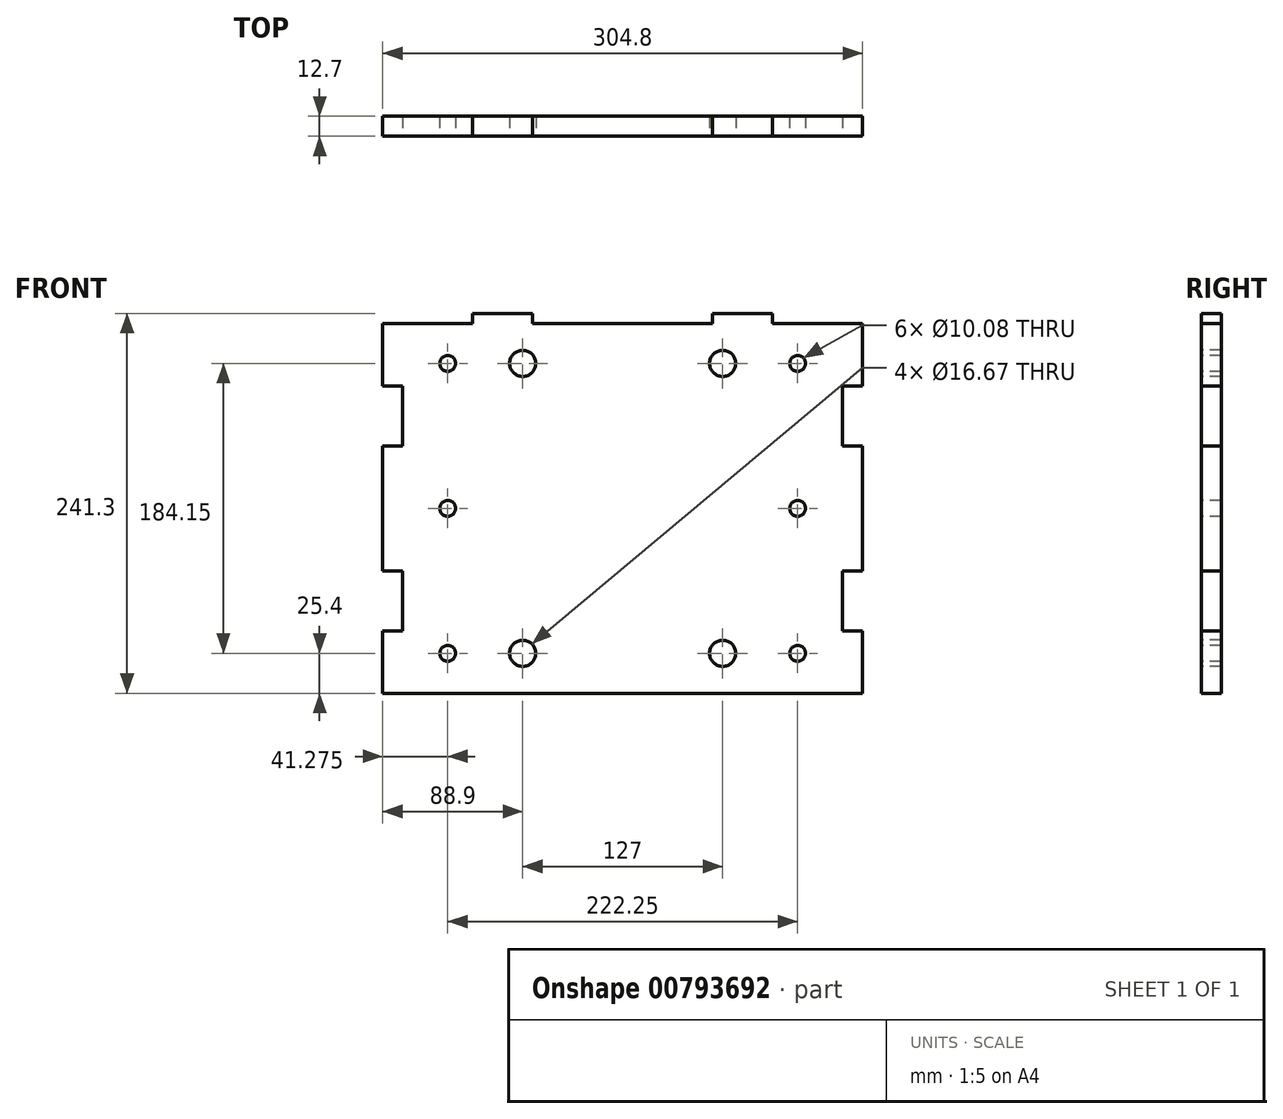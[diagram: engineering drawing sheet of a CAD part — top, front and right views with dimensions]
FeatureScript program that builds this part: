
annotation { "Feature Type Name" : "Feature", "Feature Type Description" : "" }
export const myFeature = defineFeature(function(context is Context, id is Id, definition is map)
    precondition{}
    {
        {
            var Q0;
            Q0=qCreatedBy(makeId("Front.planeOp"),FACE);
            var sketch = newSketch(context, id + "F0", { "sketchPlane" : qUnion([Q0])});
            skLineSegment(sketch, "E0.bottom", {"start": v(0, 0) * mm, "end": v(304.8, 0) * mm});
            skLineSegment(sketch, "E0.top", {"start": v(0, 234.95) * mm, "end": v(304.8, 234.95) * mm});
            skLineSegment(sketch, "E0.left", {"start": v(0, 0) * mm, "end": v(0, 234.95) * mm});
            skLineSegment(sketch, "E0.right", {"start": v(304.8, 0) * mm, "end": v(304.8, 234.95) * mm});
            skSolve(sketch);
        }
        {
            var Q0;
            Q0 = qSketchRegion(id + "F0", true);
            extrude(context, id + "F1", {"entities" : qUnion([Q0]), "depth" : 12.7 * mm, "offsetDistance" : 25.4 * mm});
        }
        {
            var Q0;
            Q0=makeQuery(id+"F1.opExtrude","CAP_FACE",FACE,{"disambiguationData":[OSD([sQuery(id+"F0.wireOp",EDGE,"E0.bottom"),sQuery(id+"F0.wireOp",EDGE,"E0.top"),sQuery(id+"F0.wireOp",EDGE,"E0.left"),sQuery(id+"F0.wireOp",EDGE,"E0.right")])],"isStart":false});
            var sketch = newSketch(context, id + "F2", { "sketchPlane" : qUnion([Q0])});
            skLineSegment(sketch, "E1", {"start": v(152.4, 0) * mm, "end": v(152.4, 234.95) * mm, "construction": true});
            skLineSegment(sketch, "E2", {"start": v(0, 25.4) * mm, "end": v(304.8, 25.4) * mm, "construction": true});
            skLineSegment(sketch, "E3", {"start": v(0, 209.55) * mm, "end": v(304.8, 209.55) * mm, "construction": true});
            skPoint(sketch, "E4", {"position": v(88.9, 209.55) * mm});
            skPoint(sketch, "E5", {"position": v(88.9, 25.4) * mm});
            skPoint(sketch, "E6.MirrorP", {"position": v(215.9, 25.4) * mm});
            skPoint(sketch, "E7.MirrorP", {"position": v(215.9, 209.55) * mm});
            skSolve(sketch);
        }
        {
            var Q0;
            Q0=sQuery(id+"F2.wireOp",VERTEX,"E6.MirrorP");
            var Q1;
            Q1=sQuery(id+"F2.wireOp",VERTEX,"E5");
            var Q2;
            Q2=sQuery(id+"F2.wireOp",VERTEX,"E4");
            var Q3;
            Q3=sQuery(id+"F2.wireOp",VERTEX,"E7.MirrorP");
            var Q4;
            Q4=makeQuery(id+"F1.opExtrude","SWEPT_BODY",BODY,{"disambiguationData":[OSD([sQuery(id+"F0.wireOp",EDGE,"E0.bottom"),sQuery(id+"F0.wireOp",EDGE,"E0.top"),sQuery(id+"F0.wireOp",EDGE,"E0.left"),sQuery(id+"F0.wireOp",EDGE,"E0.right")])]});
            hole(context, id + "F3", {"style" : HoleStyle.SIMPLE, "endStyle" : HoleEndStyle.THROUGH, "standardTappedOrClearance" : lookupTablePath({ "fit" : "Normal (ASME)", "standard" : "ANSI", "size" : "5/8", "type" : "Clearance" }), "standardBlindInLast" : lookupTablePath({ "fit" : "Free", "standard" : "ANSI", "size" : "5/8", "type" : "Clearance" }), "holeDiameter" : 16.67 * mm, "majorDiameter" : 6.35 * mm, "isTappedThrough" : true, "tappedDepth" : 12.7 * mm, "tapClearance" : 3, "locations" : qUnion([Q0, Q1, Q2, Q3]), "scope" : qUnion([Q4])});
        }
        {
            var Q0;
            Q0=makeQuery(id+"F1.opExtrude","CAP_FACE",FACE,{"disambiguationData":[OSD([sQuery(id+"F0.wireOp",EDGE,"E0.bottom"),sQuery(id+"F0.wireOp",EDGE,"E0.top"),sQuery(id+"F0.wireOp",EDGE,"E0.left"),sQuery(id+"F0.wireOp",EDGE,"E0.right")])],"isStart":false});
            var sketch = newSketch(context, id + "F4", { "sketchPlane" : qUnion([Q0])});
            skLineSegment(sketch, "E8", {"start": v(152.4, 234.95) * mm, "end": v(152.4, 0) * mm, "construction": true});
            skLineSegment(sketch, "E9", {"start": v(263.52, 234.95) * mm, "end": v(263.53, 0) * mm, "construction": true});
            skPoint(sketch, "E10", {"position": v(263.53, 209.55) * mm});
            skPoint(sketch, "E11", {"position": v(263.53, 25.4) * mm});
            skPoint(sketch, "E12", {"position": v(263.53, 117.47) * mm});
            skPoint(sketch, "E13.MirrorP", {"position": v(41.27, 25.4) * mm});
            skPoint(sketch, "E14.MirrorP", {"position": v(41.27, 117.47) * mm});
            skPoint(sketch, "E15.MirrorP", {"position": v(41.28, 209.55) * mm});
            skSolve(sketch);
        }
        {
            var Q0;
            Q0=sQuery(id+"F4.wireOp",VERTEX,"E11");
            var Q1;
            Q1=sQuery(id+"F4.wireOp",VERTEX,"E10");
            var Q2;
            Q2=sQuery(id+"F4.wireOp",VERTEX,"E15.MirrorP");
            var Q3;
            Q3=sQuery(id+"F4.wireOp",VERTEX,"E13.MirrorP");
            var Q4;
            Q4=sQuery(id+"F4.wireOp",VERTEX,"E14.MirrorP");
            var Q5;
            Q5=sQuery(id+"F4.wireOp",VERTEX,"E12");
            var Q6;
            Q6=makeQuery(id+"F1.opExtrude","SWEPT_BODY",BODY,{"disambiguationData":[OSD([sQuery(id+"F0.wireOp",EDGE,"E0.bottom"),sQuery(id+"F0.wireOp",EDGE,"E0.top"),sQuery(id+"F0.wireOp",EDGE,"E0.left"),sQuery(id+"F0.wireOp",EDGE,"E0.right")])]});
            hole(context, id + "F5", {"style" : HoleStyle.SIMPLE, "endStyle" : HoleEndStyle.THROUGH, "standardTappedOrClearance" : lookupTablePath({ "fit" : "Normal (ASME)", "standard" : "ANSI", "size" : "3/8", "type" : "Clearance" }), "standardBlindInLast" : lookupTablePath({ "fit" : "Free", "standard" : "ANSI", "size" : "3/8", "type" : "Clearance" }), "holeDiameter" : 10.08 * mm, "majorDiameter" : 6.35 * mm, "isTappedThrough" : true, "tappedDepth" : 12.7 * mm, "tapClearance" : 3, "locations" : qUnion([Q0, Q1, Q2, Q3, Q4, Q5]), "scope" : qUnion([Q6])});
        }
        {
            var Q0;
            Q0=makeQuery(id+"F1.opExtrude","CAP_FACE",FACE,{"disambiguationData":[OSD([sQuery(id+"F0.wireOp",EDGE,"E0.bottom"),sQuery(id+"F0.wireOp",EDGE,"E0.top"),sQuery(id+"F0.wireOp",EDGE,"E0.left"),sQuery(id+"F0.wireOp",EDGE,"E0.right")])],"isStart":false});
            var sketch = newSketch(context, id + "F6", { "sketchPlane" : qUnion([Q0])});
            skLineSegment(sketch, "E16", {"start": v(0, 117.47) * mm, "end": v(304.8, 117.47) * mm, "construction": true});
            skLineSegment(sketch, "E17", {"start": v(152.4, 234.95) * mm, "end": v(152.4, 0) * mm, "construction": true});
            skLineSegment(sketch, "E18.bottom", {"start": v(304.8, 195.26) * mm, "end": v(292.1, 195.26) * mm});
            skLineSegment(sketch, "E18.top", {"start": v(304.8, 157.16) * mm, "end": v(292.1, 157.16) * mm});
            skLineSegment(sketch, "E18.left", {"start": v(304.8, 195.26) * mm, "end": v(304.8, 157.16) * mm});
            skLineSegment(sketch, "E18.right", {"start": v(292.1, 195.26) * mm, "end": v(292.1, 157.16) * mm});
            skLineSegment(sketch, "E19.MirrorCS", {"start": v(304.8, 39.69) * mm, "end": v(304.8, 77.79) * mm});
            skLineSegment(sketch, "E20.MirrorCS", {"start": v(292.1, 39.69) * mm, "end": v(292.1, 77.79) * mm});
            skLineSegment(sketch, "E21.MirrorCS", {"start": v(304.8, 77.79) * mm, "end": v(292.1, 77.79) * mm});
            skLineSegment(sketch, "E22.MirrorCS", {"start": v(304.8, 39.69) * mm, "end": v(292.1, 39.69) * mm});
            skLineSegment(sketch, "E23.MirrorCS", {"start": v(0, 77.79) * mm, "end": v(12.7, 77.79) * mm});
            skLineSegment(sketch, "E24.MirrorCS", {"start": v(12.7, 39.69) * mm, "end": v(12.7, 77.79) * mm});
            skLineSegment(sketch, "E25.MirrorCS", {"start": v(0, 39.69) * mm, "end": v(0, 77.79) * mm});
            skLineSegment(sketch, "E26.MirrorCS", {"start": v(0, 39.69) * mm, "end": v(12.7, 39.69) * mm});
            skLineSegment(sketch, "E27.MirrorCS", {"start": v(0, 157.16) * mm, "end": v(12.7, 157.16) * mm});
            skLineSegment(sketch, "E28.MirrorCS", {"start": v(0, 195.26) * mm, "end": v(0, 157.16) * mm});
            skLineSegment(sketch, "E29.MirrorCS", {"start": v(12.7, 195.26) * mm, "end": v(12.7, 157.16) * mm});
            skLineSegment(sketch, "E30.MirrorCS", {"start": v(0, 195.26) * mm, "end": v(12.7, 195.26) * mm});
            skSolve(sketch);
        }
        {
            var Q0;
            Q0=makeQuery(id+"F6.imprint","IMPRINT",FACE,{"disambiguationData":[TD([[makeQuery(id+"F6.imprint","IMPRINT",EDGE,{"derivedFrom":sQuery(id+"F6.wireOp",EDGE,"E21.MirrorCS")}),1.0]])]});
            var Q1;
            Q1=makeQuery(id+"F6.imprint","IMPRINT",FACE,{"disambiguationData":[TD([[makeQuery(id+"F6.imprint","IMPRINT",EDGE,{"derivedFrom":sQuery(id+"F6.wireOp",EDGE,"E23.MirrorCS")}),-1.0]])]});
            var Q2;
            Q2=makeQuery(id+"F6.imprint","IMPRINT",FACE,{"disambiguationData":[TD([[makeQuery(id+"F6.imprint","IMPRINT",EDGE,{"derivedFrom":sQuery(id+"F6.wireOp",EDGE,"E27.MirrorCS")}),1.0]])]});
            var Q3;
            Q3=makeQuery(id+"F6.imprint","IMPRINT",FACE,{"disambiguationData":[TD([[makeQuery(id+"F6.imprint","IMPRINT",EDGE,{"derivedFrom":sQuery(id+"F6.wireOp",EDGE,"E18.bottom")}),1.0]])]});
            extrude(context, id + "F7", {"entities" : qUnion([Q0, Q1, Q2, Q3]), "operationType" : NewBodyOperationType.REMOVE, "oppositeDirection" : true, "depth" : 25.4 * mm, "offsetDistance" : 25.4 * mm});
        }
        {
            var Q0;
            Q0=makeQuery(id+"F1.opExtrude","CAP_FACE",FACE,{"disambiguationData":[OSD([sQuery(id+"F0.wireOp",EDGE,"E0.bottom"),sQuery(id+"F0.wireOp",EDGE,"E0.top"),sQuery(id+"F0.wireOp",EDGE,"E0.left"),sQuery(id+"F0.wireOp",EDGE,"E0.right")])],"isStart":false});
            var sketch = newSketch(context, id + "F8", { "sketchPlane" : qUnion([Q0])});
            skLineSegment(sketch, "E31", {"start": v(152.4, 234.95) * mm, "end": v(152.4, 0) * mm, "construction": true});
            skLineSegment(sketch, "E32", {"start": v(0, 117.48) * mm, "end": v(304.8, 117.47) * mm, "construction": true});
            skLineSegment(sketch, "E33.MirrorCS", {"start": v(95.25, 234.95) * mm, "end": v(57.15, 234.95) * mm});
            skLineSegment(sketch, "E34.MirrorCS", {"start": v(95.25, 241.3) * mm, "end": v(57.15, 241.3) * mm});
            skLineSegment(sketch, "E35.MirrorCS", {"start": v(95.25, 234.95) * mm, "end": v(95.25, 241.3) * mm});
            skLineSegment(sketch, "E36.MirrorCS", {"start": v(57.15, 234.95) * mm, "end": v(57.15, 241.3) * mm});
            skLineSegment(sketch, "E37.MirrorCS", {"start": v(247.65, 234.95) * mm, "end": v(247.65, 241.3) * mm});
            skLineSegment(sketch, "E38.MirrorCS", {"start": v(209.55, 241.3) * mm, "end": v(247.65, 241.3) * mm});
            skLineSegment(sketch, "E39.MirrorCS", {"start": v(209.55, 234.95) * mm, "end": v(247.65, 234.95) * mm});
            skLineSegment(sketch, "E40.MirrorCS", {"start": v(209.55, 234.95) * mm, "end": v(209.55, 241.3) * mm});
            skSolve(sketch);
        }
        {
            var Q0;
            Q0 = qSketchRegion(id + "F8", true);
            extrude(context, id + "F9", {"entities" : qUnion([Q0]), "operationType" : NewBodyOperationType.ADD, "oppositeDirection" : true, "depth" : 12.7 * mm, "offsetDistance" : 25.4 * mm});
        }
    });
